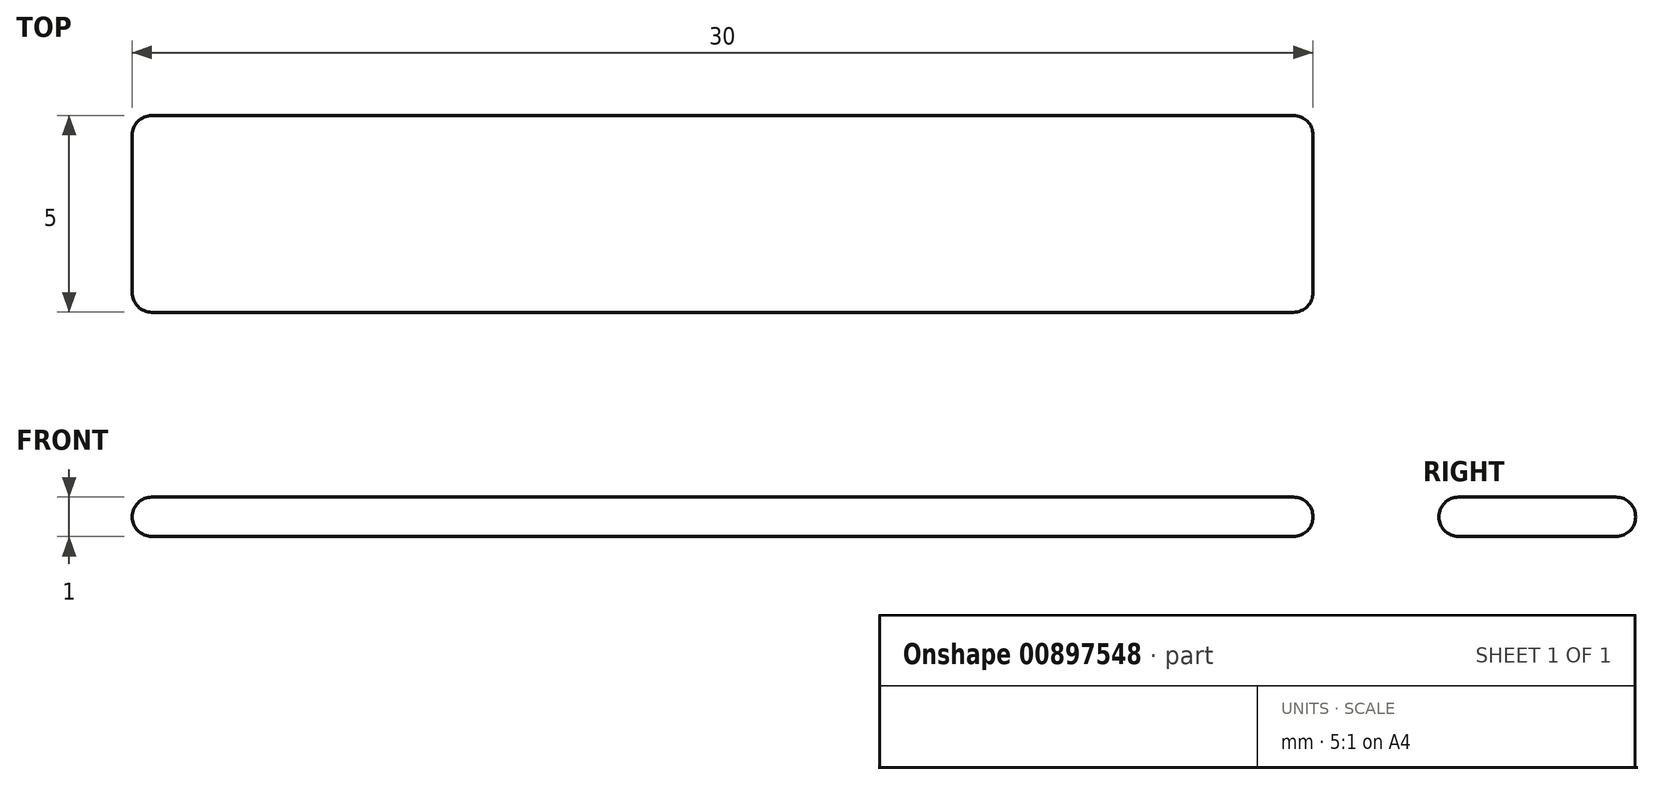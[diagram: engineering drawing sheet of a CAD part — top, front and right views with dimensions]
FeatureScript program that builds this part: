
annotation { "Feature Type Name" : "Feature", "Feature Type Description" : "" }
export const myFeature = defineFeature(function(context is Context, id is Id, definition is map)
    precondition{}
    {
        {
            var Q0;
            Q0=qCreatedBy(makeId("Top.planeOp"),FACE);
            var sketch = newSketch(context, id + "F0", { "sketchPlane" : qUnion([Q0])});
            skLineSegment(sketch, "E0.bottom", {"start": v(-50.37, 23.9) * mm, "end": v(-20.37, 23.9) * mm});
            skLineSegment(sketch, "E0.top", {"start": v(-50.37, 18.9) * mm, "end": v(-20.37, 18.9) * mm});
            skLineSegment(sketch, "E0.left", {"start": v(-50.37, 23.9) * mm, "end": v(-50.37, 18.9) * mm});
            skLineSegment(sketch, "E0.right", {"start": v(-20.37, 23.9) * mm, "end": v(-20.37, 18.9) * mm});
            skSolve(sketch);
        }
        {
            var Q0;
            Q0 = qSketchRegion(id + "F0", true);
            extrude(context, id + "F1", {"entities" : qUnion([Q0]), "depth" : 1 * mm, "offsetDistance" : 25 * mm});
        }
        {
            var Q0;
            Q0=makeQuery(id+"F1.opExtrude","CAP_FACE",FACE,{"disambiguationData":[OSD([sQuery(id+"F0.wireOp",EDGE,"E0.bottom"),sQuery(id+"F0.wireOp",EDGE,"E0.top"),sQuery(id+"F0.wireOp",EDGE,"E0.left"),sQuery(id+"F0.wireOp",EDGE,"E0.right")])],"isStart":false});
            var Q1;
            Q1=makeQuery(id+"F1.opExtrude","SWEPT_FACE",FACE,{"disambiguationData":[OSD([sQuery(id+"F0.wireOp",EDGE,"E0.top")])]});
            var Q2;
            Q2=makeQuery(id+"F1.opExtrude","CAP_FACE",FACE,{"disambiguationData":[OSD([sQuery(id+"F0.wireOp",EDGE,"E0.bottom"),sQuery(id+"F0.wireOp",EDGE,"E0.top"),sQuery(id+"F0.wireOp",EDGE,"E0.left"),sQuery(id+"F0.wireOp",EDGE,"E0.right")])],"isStart":true});
            var Q3;
            Q3=makeQuery(id+"F1.opExtrude","SWEPT_FACE",FACE,{"disambiguationData":[OSD([sQuery(id+"F0.wireOp",EDGE,"E0.right")])]});
            var Q4;
            Q4=makeQuery(id+"F1.opExtrude","SWEPT_FACE",FACE,{"disambiguationData":[OSD([sQuery(id+"F0.wireOp",EDGE,"E0.bottom")])]});
            fillet(context, id + "F2", {"entities" : qUnion([Q0, Q1, Q2, Q3, Q4]), "radius" : 0.5 * mm, "tangentPropagation" : true, "allowEdgeOverflow" : false});
        }
    });
